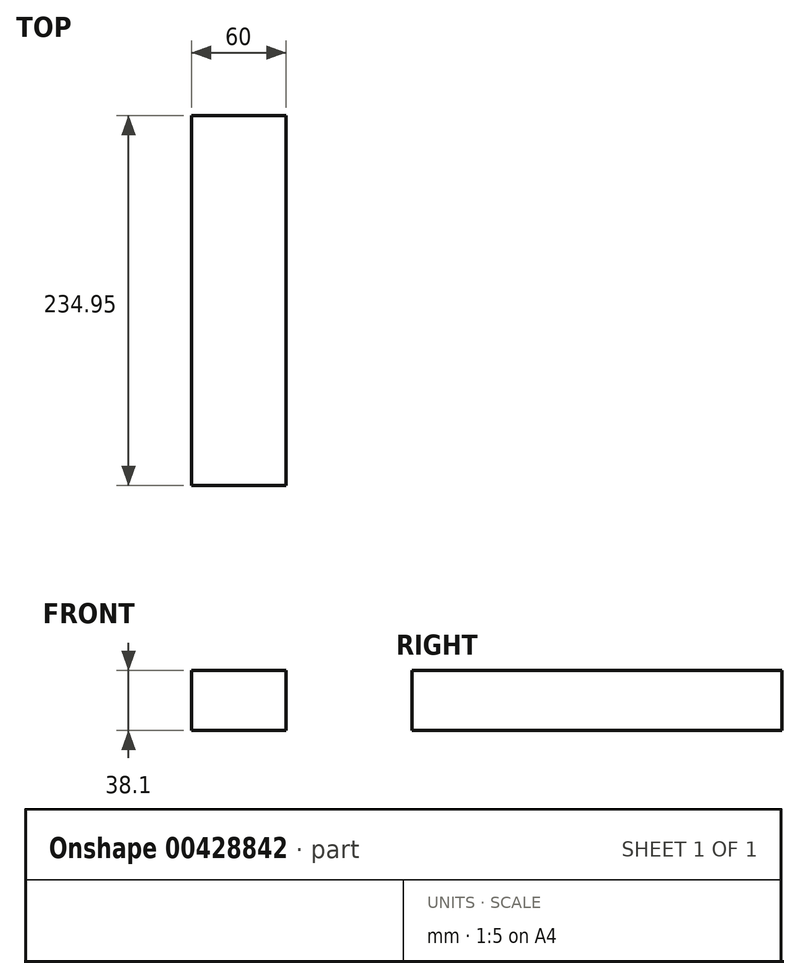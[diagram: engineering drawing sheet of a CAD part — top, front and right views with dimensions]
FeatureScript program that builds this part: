
annotation { "Feature Type Name" : "Feature", "Feature Type Description" : "" }
export const myFeature = defineFeature(function(context is Context, id is Id, definition is map)
    precondition{}
    {
        {
            assignVariable(context, id + "F0", {"name" : "Length", "anyValue" : 60});
        }
        {
            var Q0;
            Q0=qCreatedBy(makeId("Right.planeOp"),FACE);
            var sketch = newSketch(context, id + "F1", { "sketchPlane" : qUnion([Q0])});
            skLineSegment(sketch, "E0.bottom", {"start": v(124.2, 19.05) * mm, "end": v(-110.75, 19.05) * mm});
            skLineSegment(sketch, "E0.top", {"start": v(124.2, -19.05) * mm, "end": v(-110.75, -19.05) * mm});
            skLineSegment(sketch, "E0.left", {"start": v(124.2, 19.05) * mm, "end": v(124.2, -19.05) * mm});
            skLineSegment(sketch, "E0.right", {"start": v(-110.75, 19.05) * mm, "end": v(-110.75, -19.05) * mm});
            skPoint(sketch, "E0.middle", {"position": v(6.72, 0) * mm});
            skSolve(sketch);
        }
        {
            var Q0;
            Q0 = qSketchRegion(id + "F1", true);
            extrude(context, id + "F2", {"entities" : qUnion([Q0]), "depth" : (getVariable(context, 'Length')) * mm, "symmetric" : true});
        }
    });
